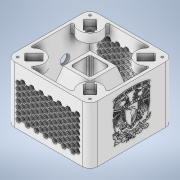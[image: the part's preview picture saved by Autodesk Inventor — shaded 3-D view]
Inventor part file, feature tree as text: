
AUTODESK INVENTOR PART (.ipt)
format: ipt  version: 2020.5 (Build 245400000, 400)  size: 6,923,264 bytes
history: mixed  units: in
note: dims shown in document units (in); Inventor stores cm internally (conversion verified against a paired STEP export)
features: extrude x1, sketch x1, mirror x1, imported_body x1
ambient origin geometry x8: Origin, YZ Plane, XZ Plane, XY Plane, X Axis, Y Axis, Z Axis, Center Point
bodies: Solid1 (imported_parasolid)
feature tree (4):
  extrude  "Extrusion1"  [1 undecoded]
  sketch  "Sketch1"  dims[d7=0.3937in d8=0.0in]
  mirror  "Simetría2"
  imported_body  NMx_Import_Brep_tag  [imported B-rep: ~115 faces, bbox_mm=[110.0, 110.0, 75.0]]
note: 1 required parameter value undecoded (feature->parameter linkage not recoverable at this tier; creation-order binding heuristic only, values carry confidence <= 0.55)
